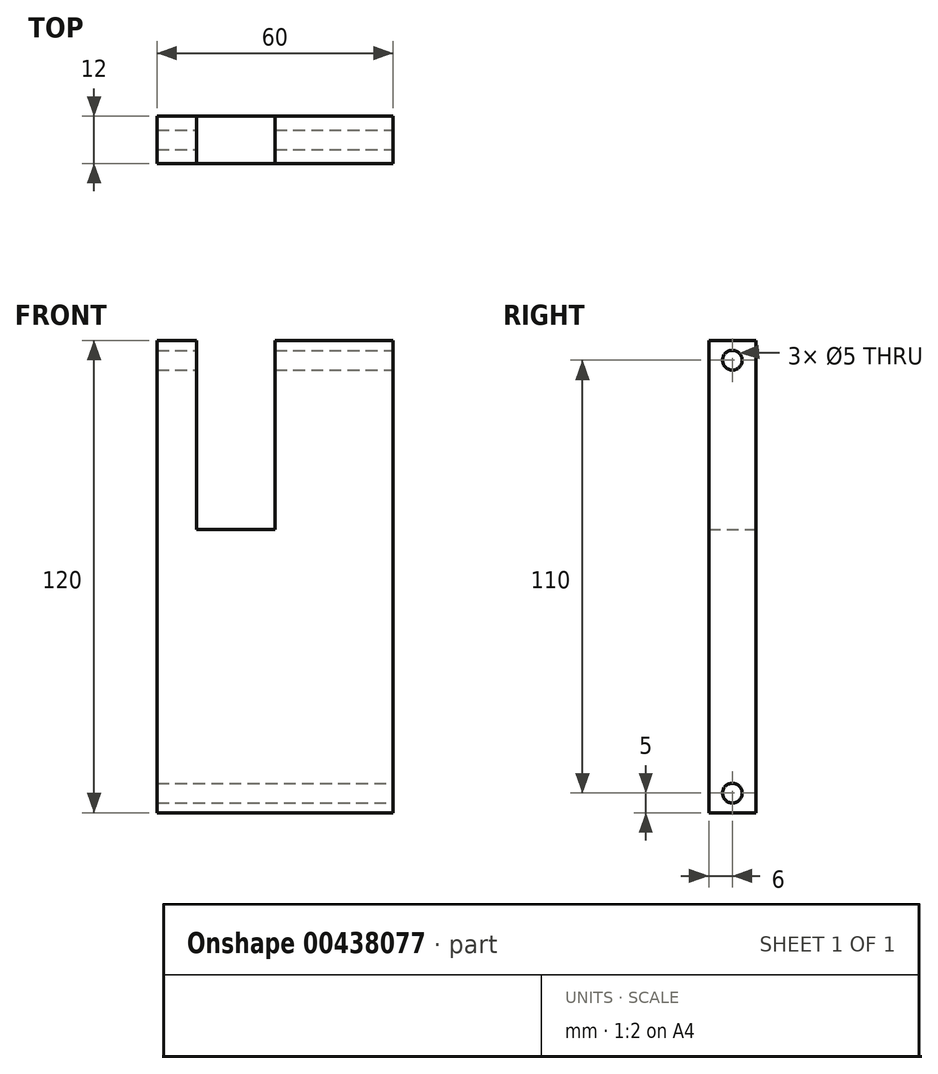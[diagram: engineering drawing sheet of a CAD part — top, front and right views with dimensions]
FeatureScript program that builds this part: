
annotation { "Feature Type Name" : "Feature", "Feature Type Description" : "" }
export const myFeature = defineFeature(function(context is Context, id is Id, definition is map)
    precondition{}
    {
        {
            var Q0;
            Q0=qCreatedBy(makeId("Front.planeOp"),FACE);
            var sketch = newSketch(context, id + "F0", { "sketchPlane" : qUnion([Q0])});
            skLineSegment(sketch, "E0.bottom", {"start": v(30, -60) * mm, "end": v(-30, -60) * mm});
            skLineSegment(sketch, "E0.top", {"start": v(30, 60) * mm, "end": v(-30, 60) * mm});
            skLineSegment(sketch, "E0.left", {"start": v(30, -60) * mm, "end": v(30, 60) * mm});
            skLineSegment(sketch, "E0.right", {"start": v(-30, -60) * mm, "end": v(-30, 60) * mm});
            skPoint(sketch, "E0.middle", {"position": v(0, 0) * mm});
            skSolve(sketch);
        }
        {
            var Q0;
            Q0=makeQuery(id+"F0.imprint","IMPRINT",FACE,{"disambiguationData":[TD([[makeQuery(id+"F0.imprint","IMPRINT",EDGE,{"derivedFrom":sQuery(id+"F0.wireOp",EDGE,"E0.bottom")}),-1.0]])]});
            var sketch = newSketch(context, id + "F1", { "sketchPlane" : qUnion([Q0])});
            skLineSegment(sketch, "E1.bottom", {"start": v(-20, 60) * mm, "end": v(0, 60) * mm});
            skLineSegment(sketch, "E1.top", {"start": v(-20, 12) * mm, "end": v(0, 12) * mm});
            skLineSegment(sketch, "E1.left", {"start": v(-20, 60) * mm, "end": v(-20, 12) * mm});
            skLineSegment(sketch, "E1.right", {"start": v(0, 60) * mm, "end": v(0, 12) * mm});
            skSolve(sketch);
        }
        {
            var Q0;
            Q0=makeQuery(id+"F0.imprint","IMPRINT",FACE,{"disambiguationData":[TD([[makeQuery(id+"F0.imprint","IMPRINT",EDGE,{"derivedFrom":sQuery(id+"F0.wireOp",EDGE,"E0.bottom")}),-1.0]])]});
            extrude(context, id + "F2", {"entities" : qUnion([Q0]), "depth" : 12 * mm});
        }
        {
            var Q0;
            Q0=makeQuery(id+"F1.imprint","IMPRINT",FACE,{"disambiguationData":[TD([[makeQuery(id+"F1.imprint","IMPRINT",EDGE,{"derivedFrom":sQuery(id+"F1.wireOp",EDGE,"E1.bottom")}),1.0]])]});
            extrude(context, id + "F3", {"entities" : qUnion([Q0]), "operationType" : NewBodyOperationType.REMOVE, "endBound" : BoundingType.UP_TO_NEXT, "depth" : 25.4 * mm});
        }
        {
            var Q0;
            Q0=makeQuery(id+"F2.opExtrude","SWEPT_FACE",FACE,{"disambiguationData":[OSD([sQuery(id+"F0.wireOp",EDGE,"E0.left")])]});
            var sketch = newSketch(context, id + "F4", { "sketchPlane" : qUnion([Q0])});
            skCircle(sketch, "E2", {"center": v(-6, 55) * mm, "radius": 2.5 * mm});
            skSolve(sketch);
        }
        {
            var Q0;
            Q0=makeQuery(id+"F4.imprint","IMPRINT",FACE,{"disambiguationData":[TD([[makeQuery(id+"F4.imprint","IMPRINT",EDGE,{"derivedFrom":sQuery(id+"F4.wireOp",EDGE,"E2")}),1.0]])]});
            var Q1;
            Q1=sQuery(id+"F4.wireOp",EDGE,"E2");
            extrude(context, id + "F5", {"entities" : qUnion([Q0]), "operationType" : NewBodyOperationType.REMOVE, "surfaceEntities" : qUnion([Q1]), "endBound" : BoundingType.THROUGH_ALL, "oppositeDirection" : true, "depth" : 25.4 * mm});
        }
        {
            var Q0;
            Q0=makeQuery(id+"F2.opExtrude","SWEPT_FACE",FACE,{"disambiguationData":[OSD([sQuery(id+"F0.wireOp",EDGE,"E0.left")])]});
            var sketch = newSketch(context, id + "F6", { "sketchPlane" : qUnion([Q0])});
            skCircle(sketch, "E3", {"center": v(-6, -55) * mm, "radius": 2.5 * mm});
            skSolve(sketch);
        }
        {
            var Q0;
            Q0=makeQuery(id+"F6.imprint","IMPRINT",FACE,{"disambiguationData":[TD([[makeQuery(id+"F6.imprint","IMPRINT",EDGE,{"derivedFrom":sQuery(id+"F6.wireOp",EDGE,"E3")}),1.0]])]});
            var Q1;
            Q1=sQuery(id+"F6.wireOp",EDGE,"E3");
            extrude(context, id + "F7", {"entities" : qUnion([Q0]), "operationType" : NewBodyOperationType.REMOVE, "surfaceEntities" : qUnion([Q1]), "oppositeDirection" : true, "depth" : 152.4 * mm});
        }
    });
